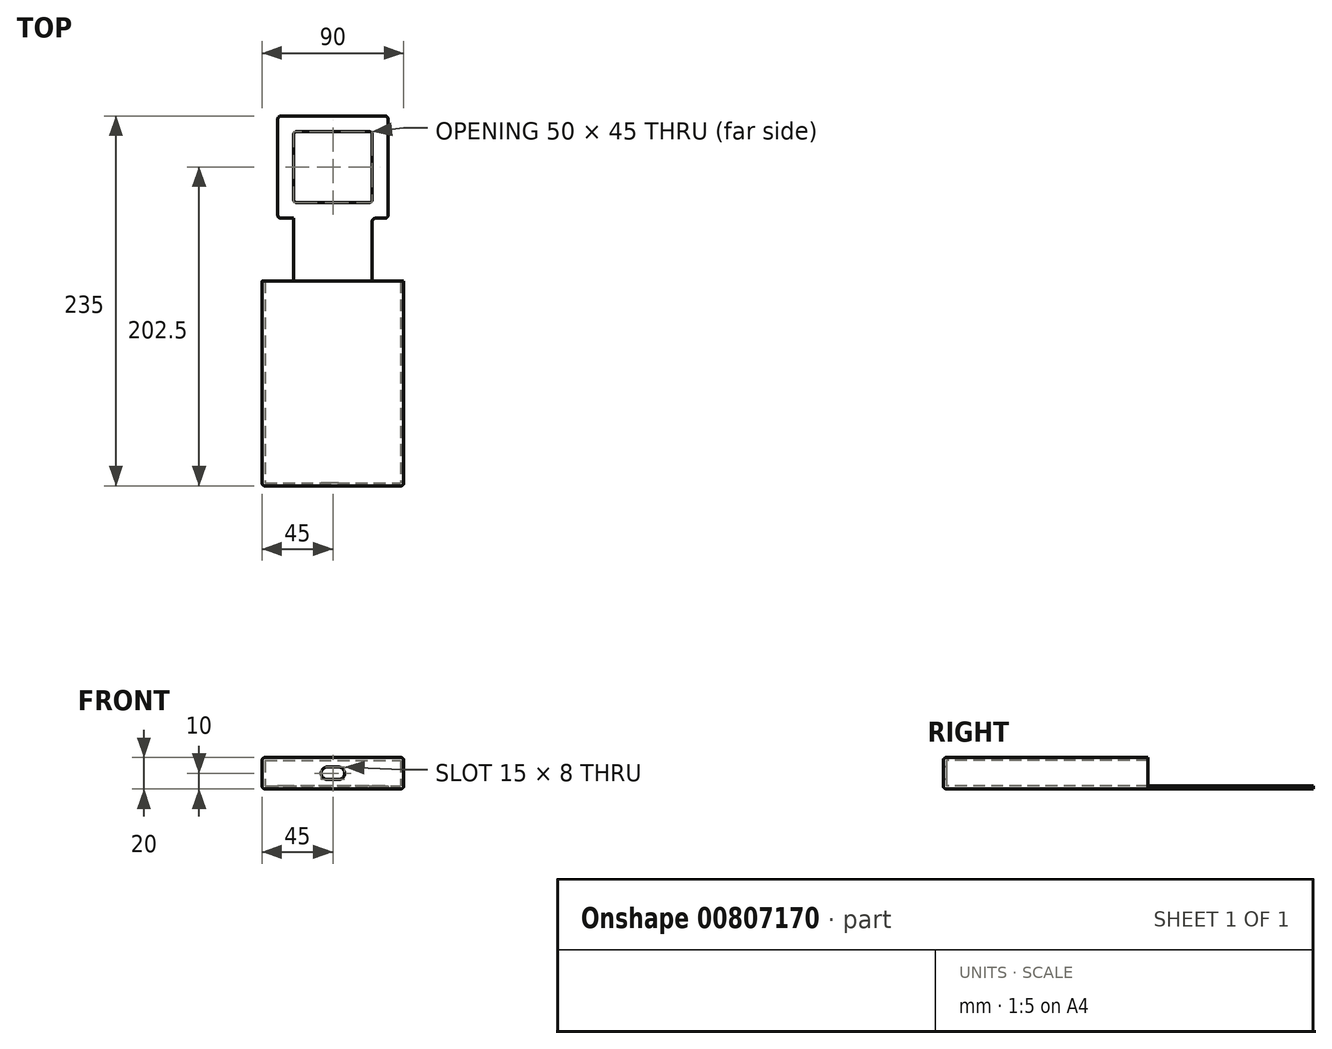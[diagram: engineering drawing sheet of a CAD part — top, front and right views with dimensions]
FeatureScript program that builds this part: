
annotation { "Feature Type Name" : "Feature", "Feature Type Description" : "" }
export const myFeature = defineFeature(function(context is Context, id is Id, definition is map)
    precondition{}
    {
        {
            var Q0;
            Q0=qCreatedBy(makeId("Top.planeOp"),FACE);
            var sketch = newSketch(context, id + "F0", { "sketchPlane" : qUnion([Q0])});
            skLineSegment(sketch, "E0.bottom", {"start": v(0, 0) * mm, "end": v(90, 0) * mm});
            skLineSegment(sketch, "E0.top", {"start": v(0, -130) * mm, "end": v(90, -130) * mm});
            skLineSegment(sketch, "E0.left", {"start": v(0, 0) * mm, "end": v(0, -130) * mm});
            skLineSegment(sketch, "E0.right", {"start": v(90, 0) * mm, "end": v(90, -130) * mm});
            skSolve(sketch);
        }
        {
            var Q0;
            Q0 = qSketchRegion(id + "F0", true);
            extrude(context, id + "F1", {"entities" : qUnion([Q0]), "depth" : 20 * mm, "offsetDistance" : 25 * mm});
        }
        {
            var Q0;
            Q0=makeQuery(id+"F1.opExtrude","SWEPT_FACE",FACE,{"disambiguationData":[OSD([sQuery(id+"F0.wireOp",EDGE,"E0.bottom")])]});
            var sketch = newSketch(context, id + "F2", { "sketchPlane" : qUnion([Q0])});
            skLineSegment(sketch, "E1.0", {"start": v(0, 0) * mm, "end": v(-90, 0) * mm});
            skLineSegment(sketch, "E2", {"start": v(-70, 0) * mm, "end": v(-70, 2) * mm});
            skLineSegment(sketch, "E3", {"start": v(-70, 2) * mm, "end": v(-20, 2) * mm});
            skLineSegment(sketch, "E4", {"start": v(-20, 2) * mm, "end": v(-20, 0) * mm});
            skSolve(sketch);
        }
        {
            var Q0;
            Q0 = qSketchRegion(id + "F2", true);
            extrude(context, id + "F3", {"entities" : qUnion([Q0]), "operationType" : NewBodyOperationType.ADD, "depth" : 40 * mm, "offsetDistance" : 25 * mm});
        }
        {
            var Q0;
            Q0=qCreatedBy(makeId("Top.planeOp"),FACE);
            var sketch = newSketch(context, id + "F4", { "sketchPlane" : qUnion([Q0])});
            skLineSegment(sketch, "E5.0", {"start": v(70, 40) * mm, "end": v(20, 40) * mm});
            skLineSegment(sketch, "E6", {"start": v(70, 40) * mm, "end": v(80, 40) * mm});
            skLineSegment(sketch, "E7", {"start": v(80, 40) * mm, "end": v(80, 105) * mm});
            skLineSegment(sketch, "E8", {"start": v(80, 105) * mm, "end": v(10, 105) * mm});
            skLineSegment(sketch, "E9", {"start": v(10, 105) * mm, "end": v(10, 40) * mm});
            skLineSegment(sketch, "E10", {"start": v(10, 40) * mm, "end": v(20, 40) * mm});
            skLineSegment(sketch, "E11.bottom", {"start": v(70, 50) * mm, "end": v(20, 50) * mm});
            skLineSegment(sketch, "E11.top", {"start": v(70, 95) * mm, "end": v(20, 95) * mm});
            skLineSegment(sketch, "E11.left", {"start": v(70, 50) * mm, "end": v(70, 95) * mm});
            skLineSegment(sketch, "E11.right", {"start": v(20, 50) * mm, "end": v(20, 95) * mm});
            skSolve(sketch);
        }
        {
            var Q0;
            Q0 = qSketchRegion(id + "F4", true);
            extrude(context, id + "F5", {"entities" : qUnion([Q0]), "operationType" : NewBodyOperationType.ADD, "depth" : 2 * mm, "offsetDistance" : 25 * mm});
        }
        {
            var Q0;
            Q0=makeQuery(id+"F1.opExtrude","SWEPT_FACE",FACE,{"disambiguationData":[OSD([sQuery(id+"F0.wireOp",EDGE,"E0.bottom")])]});
            shell(context, id + "F6", {"entities" : qUnion([Q0]), "thickness" : 2 * mm});
        }
        {
            var Q0;
            Q0=makeQuery(id+"F1.opExtrude","CAP_EDGE",EDGE,{"disambiguationData":[OSD([sQuery(id+"F0.wireOp",EDGE,"E0.left")])],"isStart":false});
            var Q1;
            Q1=makeQuery(id+"F1.opExtrude","CAP_EDGE",EDGE,{"disambiguationData":[OSD([sQuery(id+"F0.wireOp",EDGE,"E0.right")])],"isStart":false});
            var Q2;
            Q2=makeQuery(id+"F1.opExtrude","CAP_EDGE",EDGE,{"disambiguationData":[OSD([sQuery(id+"F0.wireOp",EDGE,"E0.right")])],"isStart":true});
            var Q3;
            Q3=makeQuery(id+"F1.opExtrude","CAP_EDGE",EDGE,{"disambiguationData":[OSD([sQuery(id+"F0.wireOp",EDGE,"E0.left")])],"isStart":true});
            fillet(context, id + "F7", {"entities" : qUnion([Q0, Q1, Q2, Q3]), "radius" : 2 * mm, "tangentPropagation" : true, "allowEdgeOverflow" : false});
        }
        {
            var Q0;
            Q0=makeQuery(id+"F1.opExtrude","CAP_EDGE",EDGE,{"disambiguationData":[OSD([sQuery(id+"F0.wireOp",EDGE,"E0.top")])],"isStart":true});
            fillet(context, id + "F8", {"entities" : qUnion([Q0]), "radius" : 2 * mm, "tangentPropagation" : true, "allowEdgeOverflow" : false});
        }
        {
            var Q0;
            Q0=makeQuery(id+"F5.opExtrude","SWEPT_EDGE",EDGE,{"disambiguationData":[OSD([sQuery(id+"F4.wireOp",EDGE,"E9"),sQuery(id+"F4.wireOp",EDGE,"E10")])]});
            var Q1;
            Q1=makeQuery(id+"F5.opExtrude","SWEPT_EDGE",EDGE,{"disambiguationData":[OSD([sQuery(id+"F4.wireOp",EDGE,"E8"),sQuery(id+"F4.wireOp",EDGE,"E9")])]});
            var Q2;
            Q2=makeQuery(id+"F5.opExtrude","SWEPT_EDGE",EDGE,{"disambiguationData":[OSD([sQuery(id+"F4.wireOp",EDGE,"E7"),sQuery(id+"F4.wireOp",EDGE,"E8")])]});
            var Q3;
            Q3=makeQuery(id+"F5.opExtrude","SWEPT_EDGE",EDGE,{"disambiguationData":[OSD([sQuery(id+"F4.wireOp",EDGE,"E6"),sQuery(id+"F4.wireOp",EDGE,"E7")])]});
            fillet(context, id + "F9", {"entities" : qUnion([Q0, Q1, Q2, Q3]), "radius" : 2 * mm, "tangentPropagation" : true, "allowEdgeOverflow" : false});
        }
        {
            var Q0;
            Q0=makeQuery(id+"F3.opExtrude","CAP_EDGE",EDGE,{"disambiguationData":[OSD([sQuery(id+"F2.wireOp",EDGE,"E4")])],"isStart":false});
            var Q1;
            Q1=makeQuery(id+"F3.opExtrude","CAP_EDGE",EDGE,{"disambiguationData":[OSD([sQuery(id+"F2.wireOp",EDGE,"E2")])],"isStart":false});
            var Q2;
            Q2=makeQuery(id+"F3.opExtrude","CAP_EDGE",EDGE,{"disambiguationData":[OSD([sQuery(id+"F2.wireOp",EDGE,"E2")])],"isStart":true});
            var Q3;
            Q3=makeQuery(id+"F3.opExtrude","CAP_EDGE",EDGE,{"disambiguationData":[OSD([sQuery(id+"F2.wireOp",EDGE,"E4")])],"isStart":true});
            fillet(context, id + "F10", {"entities" : qUnion([Q0, Q1, Q2, Q3]), "radius" : 2 * mm, "tangentPropagation" : true, "allowEdgeOverflow" : false});
        }
        {
            var Q0;
            Q0=makeQuery(id+"F5.opExtrude","SWEPT_EDGE",EDGE,{"disambiguationData":[OSD([sQuery(id+"F4.wireOp",EDGE,"E11.bottom"),sQuery(id+"F4.wireOp",EDGE,"E11.right")])]});
            var Q1;
            Q1=makeQuery(id+"F5.opExtrude","SWEPT_EDGE",EDGE,{"disambiguationData":[OSD([sQuery(id+"F4.wireOp",EDGE,"E11.top"),sQuery(id+"F4.wireOp",EDGE,"E11.right")])]});
            var Q2;
            Q2=makeQuery(id+"F5.opExtrude","SWEPT_EDGE",EDGE,{"disambiguationData":[OSD([sQuery(id+"F4.wireOp",EDGE,"E11.bottom"),sQuery(id+"F4.wireOp",EDGE,"E11.left")])]});
            var Q3;
            Q3=makeQuery(id+"F5.opExtrude","SWEPT_EDGE",EDGE,{"disambiguationData":[OSD([sQuery(id+"F4.wireOp",EDGE,"E11.top"),sQuery(id+"F4.wireOp",EDGE,"E11.left")])]});
            fillet(context, id + "F11", {"entities" : qUnion([Q0, Q1, Q2, Q3]), "radius" : 2 * mm, "tangentPropagation" : true, "allowEdgeOverflow" : false});
        }
        {
            var Q0;
            Q0=makeQuery(id+"F1.opExtrude","SWEPT_FACE",FACE,{"disambiguationData":[OSD([sQuery(id+"F0.wireOp",EDGE,"E0.top")])]});
            var sketch = newSketch(context, id + "F12", { "sketchPlane" : qUnion([Q0])});
            skArc(sketch, "E12", {"start": v(41.5, 14) * mm, "mid": v(37.5, 10) * mm, "end": v(41.5, 6) * mm});
            skArc(sketch, "E13", {"start": v(48.5, 6) * mm, "mid": v(52.5, 10) * mm, "end": v(48.5, 14) * mm});
            skLineSegment(sketch, "E14", {"start": v(41.5, 14) * mm, "end": v(48.5, 14) * mm});
            skLineSegment(sketch, "E15", {"start": v(41.5, 6) * mm, "end": v(48.5, 6) * mm});
            skSolve(sketch);
        }
        {
            var Q0;
            Q0 = qSketchRegion(id + "F12", true);
            extrude(context, id + "F13", {"entities" : qUnion([Q0]), "operationType" : NewBodyOperationType.REMOVE, "oppositeDirection" : true, "depth" : 25 * mm, "offsetDistance" : 25 * mm});
        }
    });
